# Revit family: Zumtobel TUBILUX LED
name_source: partatom
category: Lighting Fixtures
revit_build: Autodesk Revit 2016 (Build: 20150220_1215(x64)
units: mm (PartAtom-declared; Revit-internal decimal feet)

## family parameters
Cut with Voids When Loaded = No
Host = Face
Light Source = Yes
OmniClass Number = 23.80.70.11
OmniClass Title = Luminaries for Internal Lighting
Part Type = Normal
Room Calculation Point = No
Round Connector Dimension = Use Diameter
Shared = No

## types (15) — shared parameters
Assembly Code = D5020210
Color Filter = 16777215
Description = Tube Luminaire
Dimming Lamp Color Temperature Shift = <None>
Emit Shape Visible in Rendering = No
Glass = Zumtobel_Glass_SI
Lamp = LED
Manufacturer = Zumtobel Lighting
Tilt Angle = -90.00°
URL = http://www.zumtobel.com
zero-valued in all types: Default Elevation

## per-type parameters (varying)
| type | Apparent Load | Emit from Rectangle Length | Emit from Rectangle Width | Fixture | HO | Height | Length | Model | Photometric Web File | SLIM | Standard | Width |
| TUBILUX LED2250 L700 | 17 VA | 90 mm  [stored 0.295276 ft] | 680 mm  [stored 2.23097 ft] | Yes | No | 105 mm  [stored 0.344488 ft] | 700 mm  [stored 2.29659 ft] | 42186484 | 42186460_TUBILUX_2250_840_PM_L700_EVG.IES | No | Yes | 90 mm  [stored 0.295276 ft] |
| TUBILUX LED6400 L1540 | 50 VA | 90 mm  [stored 0.295276 ft] | 1520 mm | Yes | No | 105 mm  [stored 0.344488 ft] | 1540 mm | 42186489 | 42186465_TUBILUX_6400_840_PM_L1540_EVG.IES | No | Yes | 90 mm  [stored 0.295276 ft] |
| TUBILUX LED5400 L1540 | 40 VA | 90 mm  [stored 0.295276 ft] | 1520 mm | Yes | No | 105 mm  [stored 0.344488 ft] | 1540 mm | 42186488 | 42186464_TUBILUX_5400_840_PM_L1540_EVG.IES | No | Yes | 90 mm  [stored 0.295276 ft] |
| TUBILUX LED4900 L1260 | 37 VA | 90 mm  [stored 0.295276 ft] | 1240 mm  [stored 4.06824 ft] | Yes | No | 105 mm  [stored 0.344488 ft] | 1260 mm  [stored 4.13386 ft] | 42186487 | 42186463_TUBILUX_4900_840_PM_L1260_EVG.IES | No | Yes | 90 mm  [stored 0.295276 ft] |
| TUBILUX LED4100 L1260 | 30 VA | 90 mm  [stored 0.295276 ft] | 1240 mm  [stored 4.06824 ft] | Yes | No | 105 mm  [stored 0.344488 ft] | 1260 mm  [stored 4.13386 ft] | 42186486 | 42186462_TUBILUX_4100_840_PM_L1260_EVG.IES | No | Yes | 90 mm  [stored 0.295276 ft] |
| TUBILUX LED2700 L700 | 21 VA | 90 mm  [stored 0.295276 ft] | 680 mm  [stored 2.23097 ft] | Yes | No | 105 mm  [stored 0.344488 ft] | 700 mm  [stored 2.29659 ft] | 42186485 | 42186461_TUBILUX_2700_840_PM_L700_EVG.IES | No | Yes | 90 mm  [stored 0.295276 ft] |
| TUBILUX XT LED8300 L1260 | 67 VA | 90 mm  [stored 0.295276 ft] | 1240 mm  [stored 4.06824 ft] | Yes | No | 105 mm  [stored 0.344488 ft] | 1260 mm  [stored 4.13386 ft] | 42186407 | TUBILUX_XT_LED8300-840_PM_L1260_EVG.IES | No | Yes | 90 mm  [stored 0.295276 ft] |
| TUBILUX XT LED6200 L1260 | 47 VA | 90 mm  [stored 0.295276 ft] | 1240 mm  [stored 4.06824 ft] | Yes | No | 105 mm  [stored 0.344488 ft] | 1260 mm  [stored 4.13386 ft] | 42186406 | TUBILUX_XT_LED6200-840_PM_L1260_EVG.IES | No | Yes | 90 mm  [stored 0.295276 ft] |
| TUBILUX XT LED5400 L1260 | 40 VA | 90 mm  [stored 0.295276 ft] | 1240 mm  [stored 4.06824 ft] | Yes | No | 105 mm  [stored 0.344488 ft] | 1260 mm  [stored 4.13386 ft] | 42186405 | TUBILUX_XT_LED5400-840_PM_L1260_EVG.IES | No | Yes | 90 mm  [stored 0.295276 ft] |
| TUBILUX XT LED4500 L1260 | 32 VA | 90 mm  [stored 0.295276 ft] | 1240 mm  [stored 4.06824 ft] | Yes | No | 105 mm  [stored 0.344488 ft] | 1260 mm  [stored 4.13386 ft] | 42186404 | TUBILUX_XT_LED4500-840_PM_L1260_EVG.IES | No | Yes | 90 mm  [stored 0.295276 ft] |
| TUBILUX HO LED12000 L1530 | 84 VA | 90 mm  [stored 0.295276 ft] | 1510 mm  [stored 4.95407 ft] | No | Yes | 105 mm  [stored 0.344488 ft] | 1530 mm  [stored 5.01969 ft] | 42186446 | TUBILUX_HO_PC_LED11000-840_EVG_L1530.IES | No | Yes | 90 mm  [stored 0.295276 ft] |
| TUBILUX HO LED8500 L1530 | 64 VA | 90 mm  [stored 0.295276 ft] | 1510 mm  [stored 4.95407 ft] | No | Yes | 105 mm  [stored 0.344488 ft] | 1530 mm  [stored 5.01969 ft] | 42186445 | TUBILUX_HO_PC_LED8000-840_EVG_L1530.IES | No | Yes | 90 mm  [stored 0.295276 ft] |
| TUBILUX SLIM LED1500 L620 | 15 VA | 50 mm  [stored 0.164042 ft] | 600 mm  [stored 1.9685 ft] | No | No | 67 mm | 620 mm  [stored 2.03412 ft] | 42186447 | TUBILUX_SLIM_PC_LED1500-840_EVG_L620.IES | Yes | No | 50 mm  [stored 0.164042 ft] |
| TUBILUX SLIM LED3000 L1180 | 28 VA | 50 mm  [stored 0.164042 ft] | 1160 mm  [stored 3.80577 ft] | No | No | 67 mm | 1180 mm  [stored 3.87139 ft] | 42186448 | TUBILUX_SLIM_PC_LED3000-840_EVG_L1180.IES | Yes | No | 50 mm  [stored 0.164042 ft] |
| TUBILUX SLIM LED3700 L1460 | 31 VA | 50 mm  [stored 0.164042 ft] | 1440 mm  [stored 4.72441 ft] | No | No | 67 mm | 1460 mm  [stored 4.79003 ft] | 42186449 | TUBILUX_SLIM_PC_LED3700-840_EVG_L1460.IES | Yes | No | 50 mm  [stored 0.164042 ft] |

note: [stored X ft] marks values corroborated as IEEE doubles in the binary element streams (Revit-internal decimal feet)

## geometry (parser evidence)
native form markers: Sweep x1
no freeform markers — native parametric forms only
